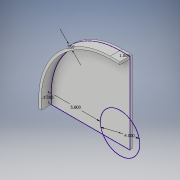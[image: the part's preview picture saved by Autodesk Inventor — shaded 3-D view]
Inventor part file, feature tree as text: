
AUTODESK INVENTOR PART (.ipt)
format: ipt  version: 2019 (Build 230136000, 136)  size: 122,368 bytes
history: native  units: in
note: dims shown in document units (in); Inventor stores cm internally (conversion verified against a paired STEP export)
features: extrude x2, sketch x1
ambient origin geometry x8: Origin, YZ Plane, XZ Plane, XY Plane, X Axis, Y Axis, Z Axis, Center Point
bodies: Solid1 (feature_tree)
feature tree (3):
  sketch  "Sketch1"  dims[d0=4.0in d1=5.0in d2=1.0in d3=1.0in d4=0.25in d5=1.0in d6=0.0in d7=0.25in d8=0.0in]
  extrude  "Extrusion1"  Depth=0.25in
  extrude  "Extrusion2"  Depth=1.0in
